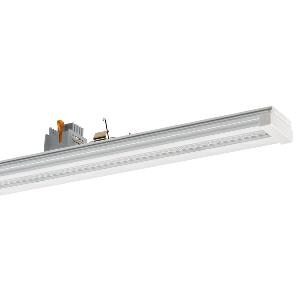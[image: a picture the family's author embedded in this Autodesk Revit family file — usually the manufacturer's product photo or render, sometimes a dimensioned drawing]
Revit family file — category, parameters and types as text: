
# Revit family: conveo_-_cvg_4500_840_w-l_da_7_226848259-00804964_f805
name_source: partatom
category: Lighting Fixtures
units: mm (PartAtom-declared; Revit-internal decimal feet)

## family parameters
Cut with Voids When Loaded = No
Host = Face
Light Source = No
Part Type = Normal
Room Calculation Point = No
Round Connector Dimension = Use Diameter
Shared = No

## types (1)
- CONVEO - CVG 4500/840/W-L/DA/7 (1 x LED, 4450 lm, 4000K)
    Apparent Load = 24 VA
    Approval mark = CE
    CIE Flux Codes = 85 97 99 100 100
    Color Rendering = 80-89
    Color Temperature = 4000K
    Control Gear = Electronic ballast
    Default Elevation = 1800 mm
    Description = CVG 4500/840/W-L/DA/7|Continuous-row system|light source: LED|work equipment: Adjustable electronic ballast, digital DALI|connected load: 220-240 V, 50-60 Hz|Power consumption: approx. 24 W|luminous flux: 4450 lm|luminous efficacy: 185 lm/W|colour temperature: Cold white, ca. 4000 K|color rendering index (CRI): >= 80|chromaticity tolerance:  3 SDCM|System of protection: IP 54|class of protection: I|technology: Continuously dimmable|luminaire body|material: Aluminium|surface: Powder coatet|colour: White|lamp cover: Acrylic (PMMA), Satine|weight (net): approx. 1.9 kg|Fastening: Available separately|maximum ambient temperature: 50 ░C|glare control: Lens optics|Approval mark: VDE - ENEC|
    Frequency = 50 Hz
    Height = 70 mm
    Lamp = 1 x LED
    Lamp Light Flux = 4450 lm
    Lamp count = 1
    Length = 1500 mm
    Luminous efficacy = 185 lm/W
    Manufacturer = Waldmann
    ModVariant = No
    Model = 226848259-00804964
    Mounting Place = Ceiling
    Mounting Type = Pendant
    Number of Poles = 1
    OnlyDefault = Yes
    Power Factor = 1
    Product Name = CONVEO - CVG 4500/840/W-L/DA/7
    Product group = Continuous-row system (industry)
    ProductGroupID = 301
    Protection Class = Protection class I
    Protection Degree = IP 54
    RLX_Detail_Level = 1
    RlxData = <blob elided: 100189 chars, md5=5a90054a>
    Socket = socket
    Standby Power = 0 W
    System Light Flux = 4450 lm
    System Power = 24 W
    Type Comments = Product without accessories
    Type Image = 226848259-00804964_1l7.jpg
    URL = http://relux.com
    VarID = ---
    Voltage = 230 V
    Voltage Range = 220-240 V
    Weight = 0.00 kg
    Width = 64 mm

## geometry (parser evidence)
native form markers: Blend x4, Sweep x10
no freeform markers — native parametric forms only
